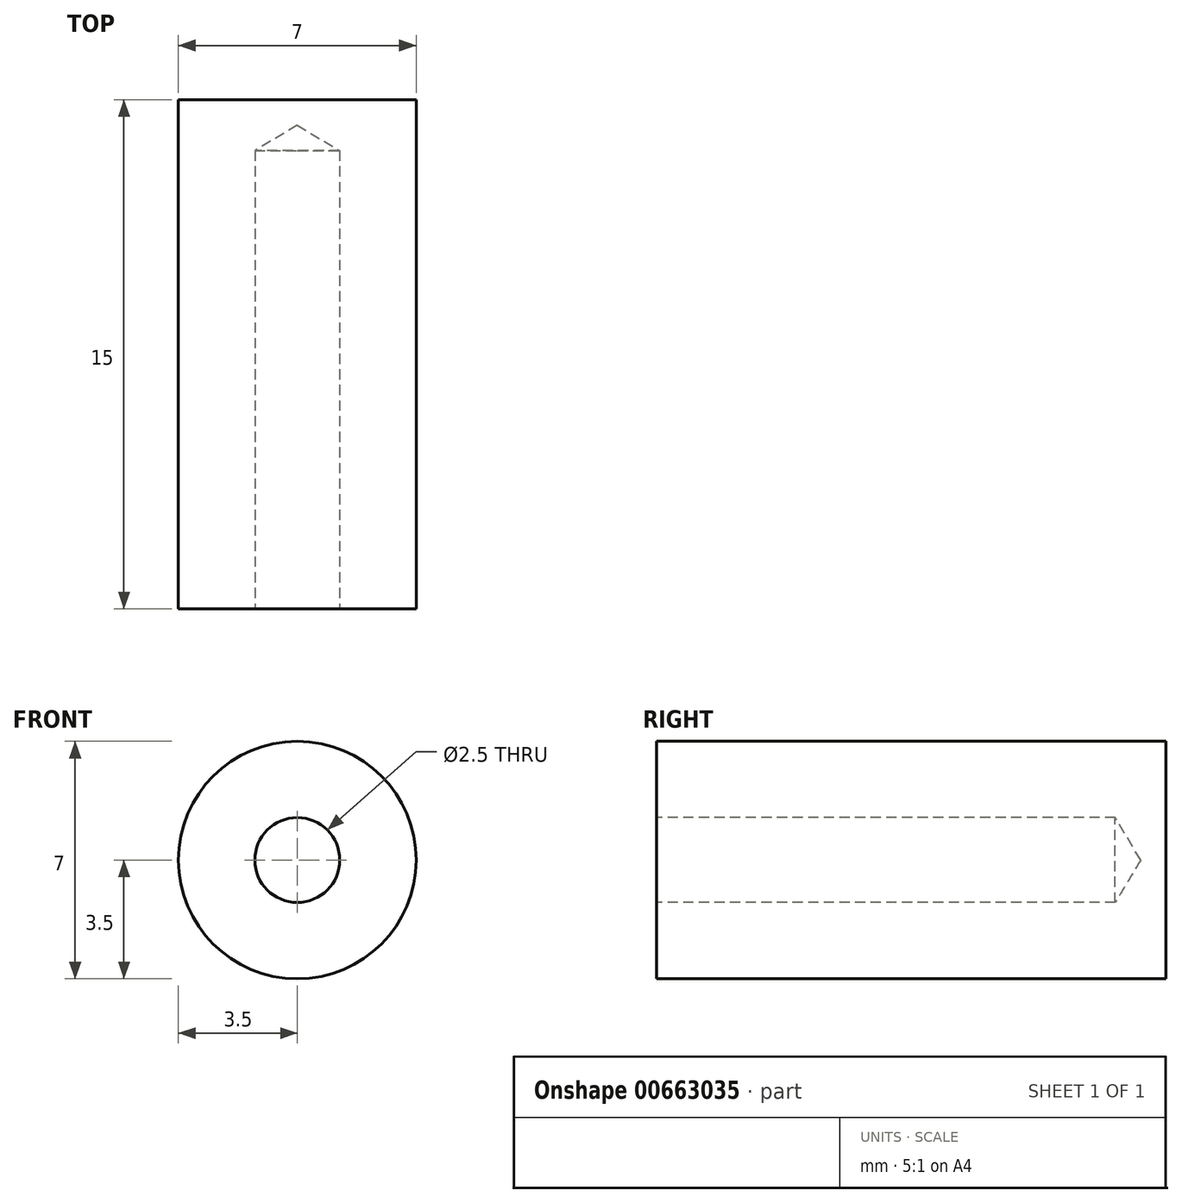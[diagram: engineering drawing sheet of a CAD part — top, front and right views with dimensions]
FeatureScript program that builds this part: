
annotation { "Feature Type Name" : "Feature", "Feature Type Description" : "" }
export const myFeature = defineFeature(function(context is Context, id is Id, definition is map)
    precondition{}
    {
        {
            var Q0;
            Q0=qCreatedBy(makeId("Front.planeOp"),FACE);
            var sketch = newSketch(context, id + "F0", { "sketchPlane" : qUnion([Q0])});
            skCircle(sketch, "E0", {"center": v(0, 0) * mm, "radius": 3.5 * mm});
            skSolve(sketch);
        }
        {
            var Q0;
            Q0=makeQuery(id+"F0.imprint","IMPRINT",FACE,{"disambiguationData":[TD([[makeQuery(id+"F0.imprint","IMPRINT",EDGE,{"derivedFrom":sQuery(id+"F0.wireOp",EDGE,"E0")}),1.0]])]});
            extrude(context, id + "F1", {"entities" : qUnion([Q0]), "depth" : 15 * mm, "offsetDistance" : 25 * mm});
        }
        {
            var Q0;
            Q0=makeQuery(id+"F1.opExtrude","CAP_FACE",FACE,{"disambiguationData":[OSD([sQuery(id+"F0.wireOp",EDGE,"E0")])],"isStart":false});
            var sketch = newSketch(context, id + "F2", { "sketchPlane" : qUnion([Q0])});
            skPoint(sketch, "E1", {"position": v(0, 0) * mm});
            skSolve(sketch);
        }
        {
            var Q0;
            Q0=sQuery(id+"F2.wireOp",VERTEX,"E1");
            var Q1;
            Q1=makeQuery(id+"F1.opExtrude","SWEPT_BODY",BODY,{"disambiguationData":[OSD([sQuery(id+"F0.wireOp",EDGE,"E0")])]});
            hole(context, id + "F3", {"style" : HoleStyle.SIMPLE, "endStyle" : HoleEndStyle.BLIND, "standardTappedOrClearance" : lookupTablePath({ "standard" : "ISO", "engagement" : "75%", "pitch" : "0.5 mm", "size" : "M3", "type" : "Tapped" }), "standardBlindInLast" : lookupTablePath({ "standard" : "ISO", "engagement" : "75%", "pitch" : "0.5 mm", "size" : "M3", "type" : "Tapped" }), "holeDiameter" : 2.5 * mm, "majorDiameter" : 3 * mm, "showTappedDepth" : true, "holeDepth" : 13.5 * mm, "isTappedThrough" : true, "tappedDepth" : 13 * mm, "tapClearance" : 1, "locations" : qUnion([Q0]), "scope" : qUnion([Q1])});
        }
    });
